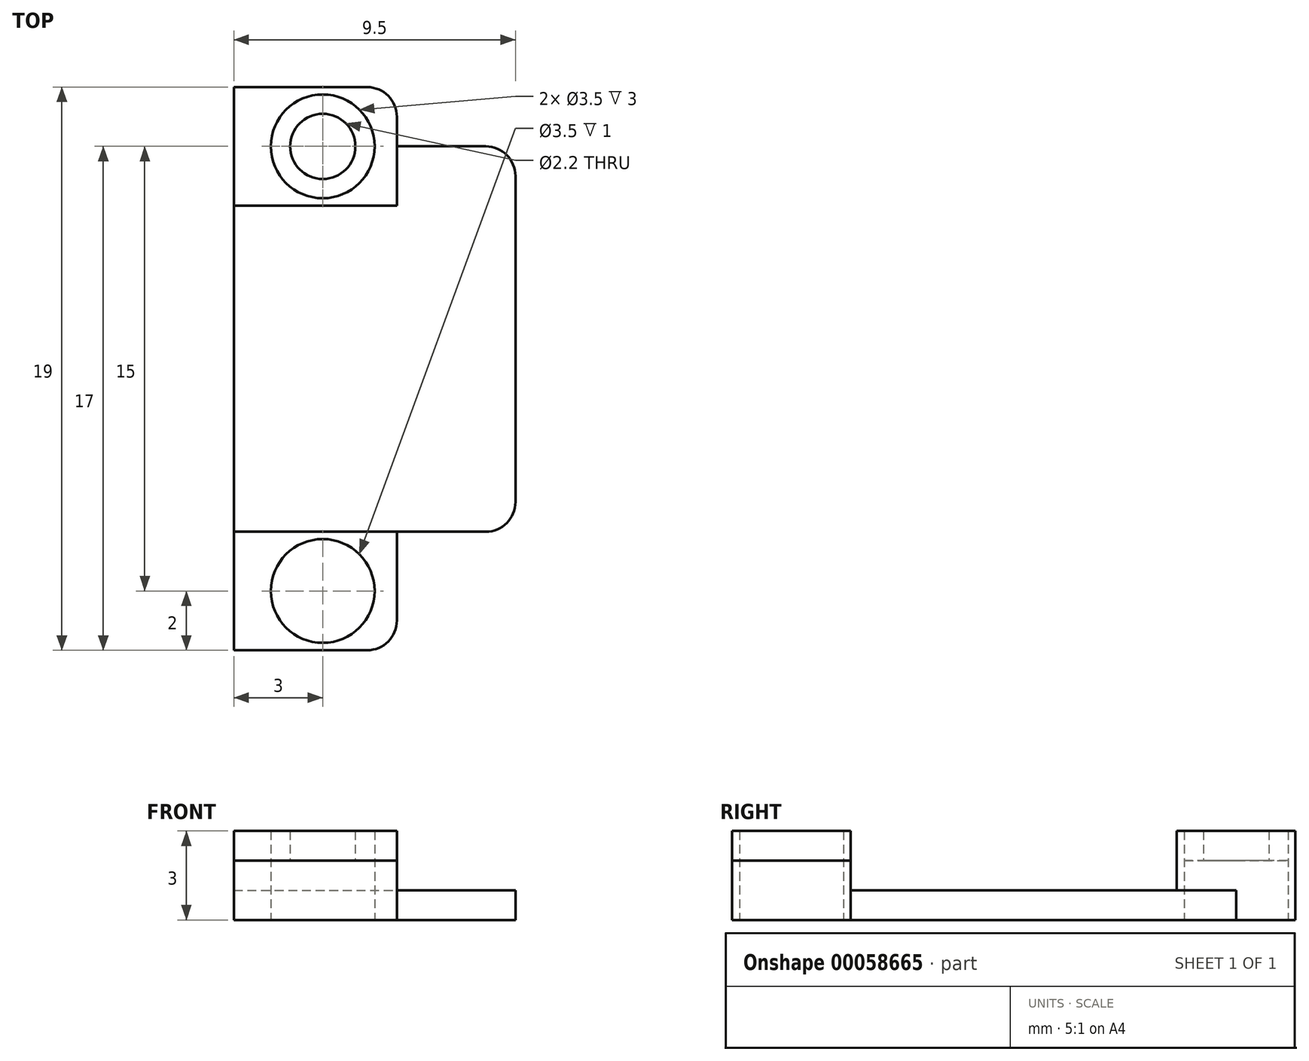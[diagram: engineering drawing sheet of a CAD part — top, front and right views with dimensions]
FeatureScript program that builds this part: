
annotation { "Feature Type Name" : "Feature", "Feature Type Description" : "" }
export const myFeature = defineFeature(function(context is Context, id is Id, definition is map)
    precondition{}
    {
        {
            var Q0;
            Q0=qCreatedBy(makeId("Top.planeOp"),FACE);
            var sketch = newSketch(context, id + "F0", { "sketchPlane" : qUnion([Q0])});
            skLineSegment(sketch, "E0.rect.bottom", {"start": v(-2.75, 9.5) * mm, "end": v(1.75, 9.5) * mm});
            skLineSegment(sketch, "E0.rect.top", {"start": v(-2.75, -9.5) * mm, "end": v(1.75, -9.5) * mm});
            skLineSegment(sketch, "E0.rect.left", {"start": v(-2.75, 9.5) * mm, "end": v(-2.75, -9.5) * mm});
            skLineSegment(sketch, "E0.rect.right", {"start": v(2.75, 8.5) * mm, "end": v(2.75, -8.5) * mm});
            skPoint(sketch, "E0.rect.middle", {"position": v(0, 0) * mm});
            skCircle(sketch, "E1", {"center": v(0.25, 7.5) * mm, "radius": 1.1 * mm});
            skCircle(sketch, "E2", {"center": v(0.25, 7.5) * mm, "radius": 1.75 * mm});
            skLineSegment(sketch, "E3", {"start": v(-2.75, 5.5) * mm, "end": v(2.75, 5.5) * mm});
            skLineSegment(sketch, "E4.MirrorCS", {"start": v(-2.75, -5.5) * mm, "end": v(2.75, -5.5) * mm});
            skCircle(sketch, "E5.MirrorC", {"center": v(0.25, -7.5) * mm, "radius": 1.75 * mm});
            skCircle(sketch, "E6.MirrorC", {"center": v(0.25, -7.5) * mm, "radius": 1.1 * mm});
            skPoint(sketch, "E7.visualSharp", {"position": v(2.75, 9.5) * mm});
            skArc(sketch, "E7.filletArc", {"start": v(2.75, 8.5) * mm, "mid": v(2.46, 9.2) * mm, "end": v(1.75, 9.5) * mm});
            skPoint(sketch, "E8.visualSharp", {"position": v(2.75, -9.5) * mm});
            skArc(sketch, "E8.filletArc", {"start": v(1.75, -9.5) * mm, "mid": v(2.46, -9.2) * mm, "end": v(2.75, -8.5) * mm});
            skLineSegment(sketch, "E9.bottom", {"start": v(2.75, -5.5) * mm, "end": v(5.75, -5.5) * mm});
            skLineSegment(sketch, "E9.top", {"start": v(2.75, 7.5) * mm, "end": v(5.75, 7.5) * mm});
            skLineSegment(sketch, "E9.left", {"start": v(2.75, -5.5) * mm, "end": v(2.75, 7.5) * mm});
            skLineSegment(sketch, "E9.right", {"start": v(6.75, -4.5) * mm, "end": v(6.75, 6.5) * mm});
            skPoint(sketch, "E10.visualSharp", {"position": v(6.75, 7.5) * mm});
            skArc(sketch, "E10.filletArc", {"start": v(6.75, 6.5) * mm, "mid": v(6.46, 7.2) * mm, "end": v(5.75, 7.5) * mm});
            skPoint(sketch, "E11.visualSharp", {"position": v(6.75, -5.5) * mm});
            skArc(sketch, "E11.filletArc", {"start": v(5.75, -5.5) * mm, "mid": v(6.46, -5.2) * mm, "end": v(6.75, -4.5) * mm});
            skSolve(sketch);
        }
        {
            var Q0;
            {var subQ0=sQuery(id+"F0.wireOp",EDGE,"E3");Q0=makeQuery(id+"F0.imprint","IMPRINT",FACE,{"disambiguationData":[TD([[makeQuery(id+"F0.imprint","IMPRINT",EDGE,{"derivedFrom":subQ0}),-1.0]])]});}
            var Q1;
            {var subQ4=sQuery(id+"F0.wireOp",EDGE,"E9.bottom");Q1=makeQuery(id+"F0.imprint","IMPRINT",FACE,{"disambiguationData":[TD([[makeQuery(id+"F0.imprint","IMPRINT",EDGE,{"derivedFrom":subQ4}),1.0]])]});}
            extrude(context, id + "F1", {"entities" : qUnion([Q0, Q1]), "depth" : 1 * mm});
        }
        {
            var Q0;
            {var subQ1=sQuery(id+"F0.wireOp",EDGE,"E0.rect.bottom");Q0=makeQuery(id+"F0.imprint","IMPRINT",FACE,{"disambiguationData":[TD([[makeQuery(id+"F0.imprint","IMPRINT",EDGE,{"derivedFrom":subQ1}),-1.0]])]});}
            var Q1;
            {var subQ2=sQuery(id+"F0.wireOp",EDGE,"E0.rect.top");Q1=makeQuery(id+"F0.imprint","IMPRINT",FACE,{"disambiguationData":[TD([[makeQuery(id+"F0.imprint","IMPRINT",EDGE,{"derivedFrom":subQ2}),1.0]])]});}
            extrude(context, id + "F2", {"entities" : qUnion([Q0, Q1]), "operationType" : NewBodyOperationType.ADD, "depth" : 3 * mm});
        }
        {
            var Q0;
            Q0=makeQuery(id+"F0.imprint","IMPRINT",FACE,{"disambiguationData":[TD([[makeQuery(id+"F0.imprint","IMPRINT",EDGE,{"derivedFrom":sQuery(id+"F0.wireOp",EDGE,"E1")}),-1.0]])]});
            var Q1;
            Q1=makeQuery(id+"F0.imprint","IMPRINT",FACE,{"disambiguationData":[TD([[makeQuery(id+"F0.imprint","IMPRINT",EDGE,{"derivedFrom":sQuery(id+"F0.wireOp",EDGE,"E5.MirrorC")}),-1.0]])]});
            extrude(context, id + "F3", {"entities" : qUnion([Q0, Q1]), "depth" : 3 * mm, "hasSecondDirection" : true, "secondDirectionOppositeDirection" : false, "secondDirectionDepth" : 2 * mm});
        }
    });
